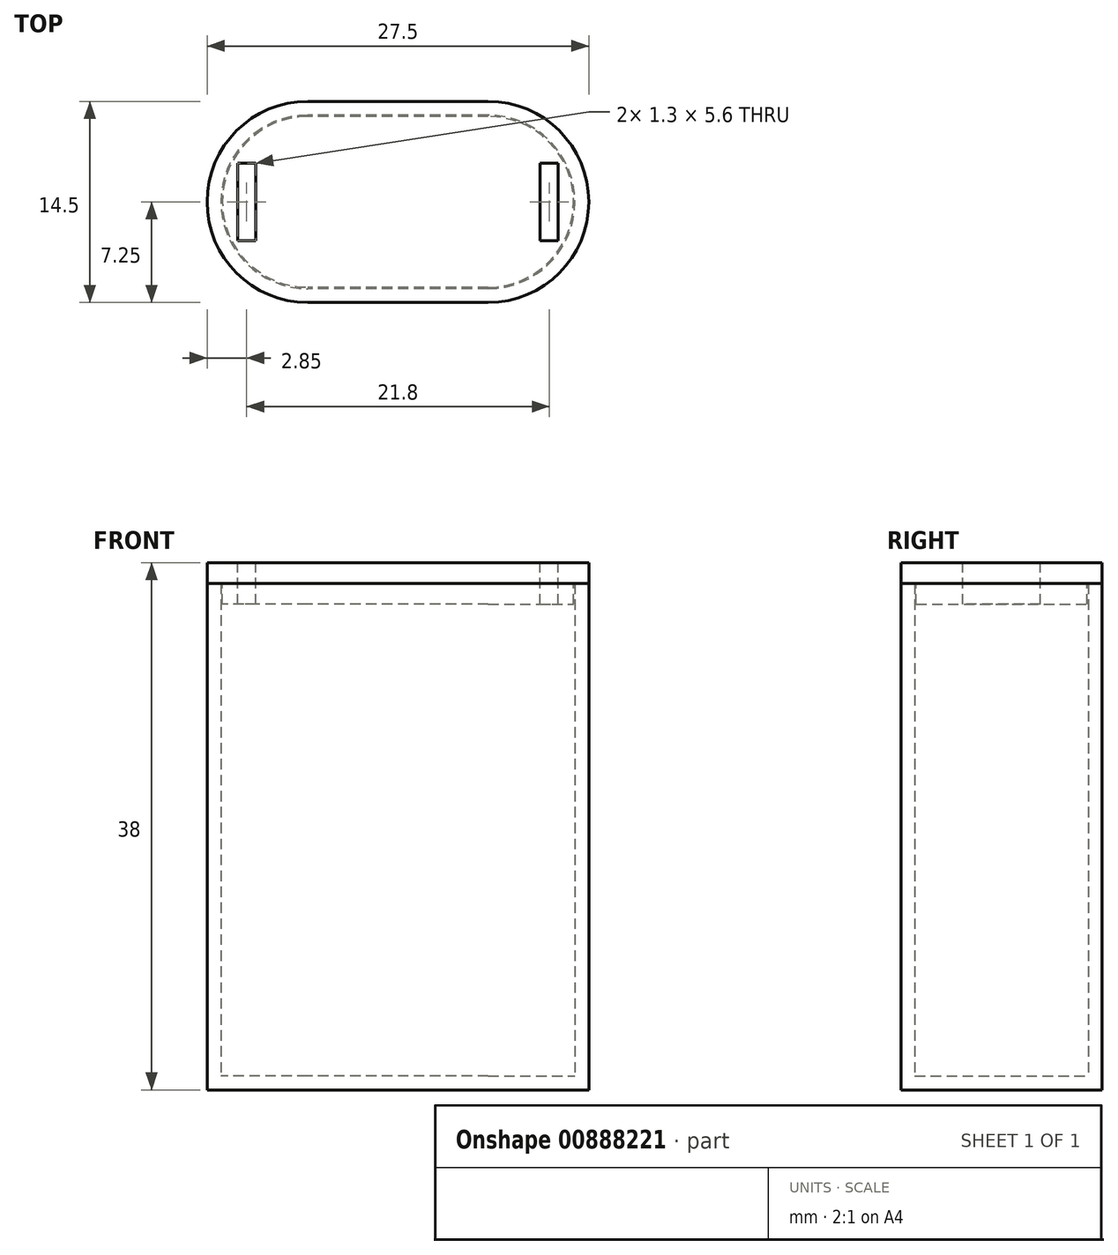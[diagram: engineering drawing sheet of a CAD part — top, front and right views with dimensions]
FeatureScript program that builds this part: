
annotation { "Feature Type Name" : "Feature", "Feature Type Description" : "" }
export const myFeature = defineFeature(function(context is Context, id is Id, definition is map)
    precondition{}
    {
        {
            var Q0;
            Q0=qCreatedBy(makeId("Top.planeOp"),FACE);
            var sketch = newSketch(context, id + "F0", { "sketchPlane" : qUnion([Q0])});
            skLineSegment(sketch, "E0.bottom", {"start": v(6.5, -7.25) * mm, "end": v(-6.5, -7.25) * mm});
            skLineSegment(sketch, "E0.top", {"start": v(6.5, 7.25) * mm, "end": v(-6.5, 7.25) * mm});
            skLineSegment(sketch, "E0.left", {"start": v(6.5, -7.25) * mm, "end": v(6.5, 7.25) * mm});
            skLineSegment(sketch, "E0.right", {"start": v(-6.5, -7.25) * mm, "end": v(-6.5, 7.25) * mm});
            skPoint(sketch, "E0.middle", {"position": v(0, 0) * mm});
            skArc(sketch, "E1", {"start": v(-6.5, 7.25) * mm, "mid": v(-13.75, 0) * mm, "end": v(-6.5, -7.25) * mm});
            skArc(sketch, "E2", {"start": v(6.5, -7.25) * mm, "mid": v(13.75, 0) * mm, "end": v(6.5, 7.25) * mm});
            skSolve(sketch);
        }
        {
            var Q0;
            Q0 = qSketchRegion(id + "F0", true);
            extrude(context, id + "F1", {"entities" : qUnion([Q0]), "depth" : 36.5 * mm, "offsetDistance" : 25 * mm});
        }
        {
            var Q0;
            Q0=makeQuery(id+"F1.opExtrude","CAP_FACE",FACE,{"disambiguationData":[OSD([sQuery(id+"F0.wireOp",EDGE,"E0.bottom"),sQuery(id+"F0.wireOp",EDGE,"E0.top"),sQuery(id+"F0.wireOp",EDGE,"E1"),sQuery(id+"F0.wireOp",EDGE,"E2")])],"isStart":false});
            shell(context, id + "F2", {"entities" : qUnion([Q0]), "thickness" : 1 * mm});
        }
        {
            var Q0;
            Q0=makeQuery(id+"F1.opExtrude","CAP_FACE",FACE,{"disambiguationData":[OSD([sQuery(id+"F0.wireOp",EDGE,"E0.bottom"),sQuery(id+"F0.wireOp",EDGE,"E0.top"),sQuery(id+"F0.wireOp",EDGE,"E1"),sQuery(id+"F0.wireOp",EDGE,"E2")])],"isStart":false});
            var sketch = newSketch(context, id + "F3", { "sketchPlane" : qUnion([Q0])});
            skLineSegment(sketch, "E3.0", {"start": v(6.5, -7.25) * mm, "end": v(-6.5, -7.25) * mm});
            skArc(sketch, "E4.0", {"start": v(-6.5, 7.25) * mm, "mid": v(-13.75, 0) * mm, "end": v(-6.5, -7.25) * mm});
            skLineSegment(sketch, "E5.0", {"start": v(6.5, 7.25) * mm, "end": v(-6.5, 7.25) * mm});
            skArc(sketch, "E6.0", {"start": v(6.5, -7.25) * mm, "mid": v(13.75, 0) * mm, "end": v(6.5, 7.25) * mm});
            skSolve(sketch);
        }
        {
            var Q0;
            Q0 = qSketchRegion(id + "F3", true);
            extrude(context, id + "F4", {"entities" : qUnion([Q0]), "depth" : 1.5 * mm, "offsetDistance" : 25 * mm});
        }
        {
            var Q0;
            Q0=makeQuery(id+"F4.opExtrude","CAP_FACE",FACE,{"disambiguationData":[OSD([sQuery(id+"F3.wireOp",EDGE,"E3.0"),sQuery(id+"F3.wireOp",EDGE,"E4.0"),sQuery(id+"F3.wireOp",EDGE,"E5.0"),sQuery(id+"F3.wireOp",EDGE,"E6.0")])],"isStart":true});
            var sketch = newSketch(context, id + "F5", { "sketchPlane" : qUnion([Q0])});
            skLineSegment(sketch, "E7.0", {"start": v(6.5, 6.25) * mm, "end": v(-6.5, 6.25) * mm, "construction": true});
            skArc(sketch, "E8.0", {"start": v(6.5, 6.25) * mm, "mid": v(12.75, 0) * mm, "end": v(6.5, -6.25) * mm, "construction": true});
            skLineSegment(sketch, "E9.0", {"start": v(6.5, -6.25) * mm, "end": v(-6.5, -6.25) * mm, "construction": true});
            skArc(sketch, "E10.0", {"start": v(-6.5, -6.25) * mm, "mid": v(-12.75, 0) * mm, "end": v(-6.5, 6.25) * mm, "construction": true});
            skArc(sketch, "E11.0", {"start": v(-6.5, -6.15) * mm, "mid": v(-12.65, 0) * mm, "end": v(-6.5, 6.15) * mm});
            skLineSegment(sketch, "E11.1", {"start": v(6.5, -6.15) * mm, "end": v(-6.5, -6.15) * mm});
            skArc(sketch, "E11.2", {"start": v(6.5, 6.15) * mm, "mid": v(12.65, 0) * mm, "end": v(6.5, -6.15) * mm});
            skLineSegment(sketch, "E11.3", {"start": v(6.5, 6.15) * mm, "end": v(-6.5, 6.15) * mm});
            skSolve(sketch);
        }
        {
            var Q0;
            Q0 = qSketchRegion(id + "F5", true);
            extrude(context, id + "F6", {"entities" : qUnion([Q0]), "operationType" : NewBodyOperationType.ADD, "depth" : 1.5 * mm, "offsetDistance" : 25 * mm});
        }
        {
            var Q0;
            Q0=makeQuery(id+"F4.opExtrude","CAP_FACE",FACE,{"disambiguationData":[OSD([sQuery(id+"F3.wireOp",EDGE,"E3.0"),sQuery(id+"F3.wireOp",EDGE,"E4.0"),sQuery(id+"F3.wireOp",EDGE,"E5.0"),sQuery(id+"F3.wireOp",EDGE,"E6.0")])],"isStart":false});
            var sketch = newSketch(context, id + "F7", { "sketchPlane" : qUnion([Q0])});
            skLineSegment(sketch, "E12.bottom", {"start": v(-10.25, 2.8) * mm, "end": v(-11.55, 2.8) * mm});
            skLineSegment(sketch, "E12.top", {"start": v(-10.25, -2.8) * mm, "end": v(-11.55, -2.8) * mm});
            skLineSegment(sketch, "E12.left", {"start": v(-10.25, 2.8) * mm, "end": v(-10.25, -2.8) * mm});
            skLineSegment(sketch, "E12.right", {"start": v(-11.55, 2.8) * mm, "end": v(-11.55, -2.8) * mm});
            skPoint(sketch, "E12.middle", {"position": v(-10.9, 0) * mm});
            skLineSegment(sketch, "E13", {"start": v(0, 0) * mm, "end": v(0, 2.55) * mm, "construction": true});
            skLineSegment(sketch, "E14.MirrorCS", {"start": v(11.55, 2.8) * mm, "end": v(11.55, -2.8) * mm});
            skLineSegment(sketch, "E15.MirrorCS", {"start": v(10.25, 2.8) * mm, "end": v(10.25, -2.8) * mm});
            skLineSegment(sketch, "E16.MirrorCS", {"start": v(10.25, 2.8) * mm, "end": v(11.55, 2.8) * mm});
            skLineSegment(sketch, "E17.MirrorCS", {"start": v(10.25, -2.8) * mm, "end": v(11.55, -2.8) * mm});
            skPoint(sketch, "E18.MirrorP", {"position": v(10.9, 0) * mm});
            skSolve(sketch);
        }
        {
            var Q0;
            Q0 = qSketchRegion(id + "F7", true);
            extrude(context, id + "F8", {"entities" : qUnion([Q0]), "operationType" : NewBodyOperationType.REMOVE, "oppositeDirection" : true, "depth" : 3 * mm, "offsetDistance" : 25 * mm});
        }
    });
